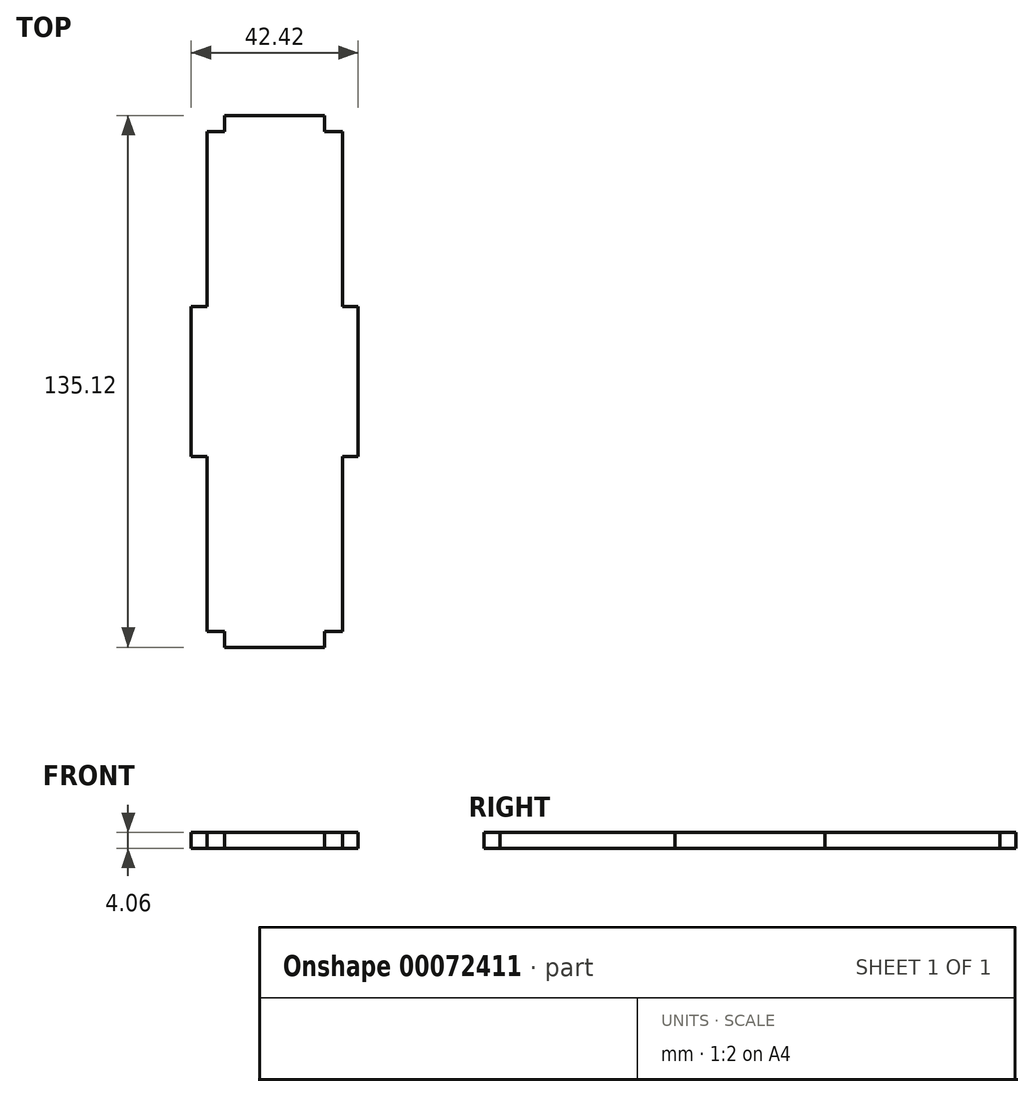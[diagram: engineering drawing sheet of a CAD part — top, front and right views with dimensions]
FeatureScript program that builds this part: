
annotation { "Feature Type Name" : "Feature", "Feature Type Description" : "" }
export const myFeature = defineFeature(function(context is Context, id is Id, definition is map)
    precondition{}
    {
        {
            var Q0;
            Q0=qCreatedBy(makeId("Top.planeOp"),FACE);
            var sketch = newSketch(context, id + "F0", { "sketchPlane" : qUnion([Q0])});
            skLineSegment(sketch, "E0.rect.bottom", {"start": v(17.14, 63.5) * mm, "end": v(-17.15, 63.5) * mm});
            skLineSegment(sketch, "E0.rect.top", {"start": v(17.14, -63.5) * mm, "end": v(-17.15, -63.5) * mm});
            skLineSegment(sketch, "E0.rect.left", {"start": v(17.15, 63.5) * mm, "end": v(17.15, -63.5) * mm});
            skLineSegment(sketch, "E0.rect.right", {"start": v(-17.15, 63.5) * mm, "end": v(-17.15, -63.5) * mm});
            skPoint(sketch, "E0.rect.middle", {"position": v(0, 0) * mm});
            skLineSegment(sketch, "E1.rect.bottom", {"start": v(12.7, -67.56) * mm, "end": v(-12.7, -67.56) * mm});
            skLineSegment(sketch, "E1.rect.top", {"start": v(12.7, -59.44) * mm, "end": v(-12.7, -59.44) * mm});
            skLineSegment(sketch, "E1.rect.left", {"start": v(12.7, -67.56) * mm, "end": v(12.7, -59.44) * mm});
            skLineSegment(sketch, "E1.rect.right", {"start": v(-12.7, -67.56) * mm, "end": v(-12.7, -59.44) * mm});
            skPoint(sketch, "E1.rect.middle", {"position": v(0, -63.5) * mm});
            skLineSegment(sketch, "E2", {"start": v(-58.3, 0) * mm, "end": v(70.6, 0) * mm, "construction": true});
            skLineSegment(sketch, "E3", {"start": v(0, 86.83) * mm, "end": v(0, -101.23) * mm, "construction": true});
            skPoint(sketch, "E3.startSnap0", {"position": v(0, 63.5) * mm});
            skLineSegment(sketch, "E4.MirrorCS", {"start": v(12.7, 59.44) * mm, "end": v(-12.7, 59.44) * mm});
            skLineSegment(sketch, "E5.MirrorCS", {"start": v(12.7, 67.56) * mm, "end": v(-12.7, 67.56) * mm});
            skLineSegment(sketch, "E6.MirrorCS", {"start": v(-12.7, 67.56) * mm, "end": v(-12.7, 59.44) * mm});
            skLineSegment(sketch, "E7.MirrorCS", {"start": v(12.7, 67.56) * mm, "end": v(12.7, 59.44) * mm});
            skLineSegment(sketch, "E8.rect.bottom", {"start": v(21.2, 19.05) * mm, "end": v(13.08, 19.05) * mm});
            skLineSegment(sketch, "E8.rect.top", {"start": v(21.2, -19.05) * mm, "end": v(13.08, -19.05) * mm});
            skLineSegment(sketch, "E8.rect.left", {"start": v(21.2, 19.05) * mm, "end": v(21.2, -19.05) * mm});
            skLineSegment(sketch, "E8.rect.right", {"start": v(13.08, 19.05) * mm, "end": v(13.08, -19.05) * mm});
            skPoint(sketch, "E8.rect.middle", {"position": v(17.15, 0) * mm});
            skLineSegment(sketch, "E9.MirrorCS", {"start": v(-13.08, 19.05) * mm, "end": v(-13.08, -19.05) * mm});
            skLineSegment(sketch, "E10.MirrorCS", {"start": v(-21.2, 19.05) * mm, "end": v(-13.08, 19.05) * mm});
            skLineSegment(sketch, "E11.MirrorCS", {"start": v(-21.2, 19.05) * mm, "end": v(-21.2, -19.05) * mm});
            skLineSegment(sketch, "E12.MirrorCS", {"start": v(-21.2, -19.05) * mm, "end": v(-13.08, -19.05) * mm});
            skSolve(sketch);
        }
        {
            var Q0;
            {var subQ5=sQuery(id+"F0.wireOp",EDGE,"E8.rect.left");Q0=makeQuery(id+"F0.imprint","IMPRINT",FACE,{"disambiguationData":[TD([[makeQuery(id+"F0.imprint","IMPRINT",EDGE,{"derivedFrom":subQ5}),-1.0]])]});}
            var Q1;
            {var subQ5=sQuery(id+"F0.wireOp",EDGE,"E4.MirrorCS");Q1=makeQuery(id+"F0.imprint","IMPRINT",FACE,{"disambiguationData":[TD([[makeQuery(id+"F0.imprint","IMPRINT",EDGE,{"derivedFrom":subQ5}),-1.0]])]});}
            var Q2;
            {var subQ5=sQuery(id+"F0.wireOp",EDGE,"E1.rect.bottom");Q2=makeQuery(id+"F0.imprint","IMPRINT",FACE,{"disambiguationData":[TD([[makeQuery(id+"F0.imprint","IMPRINT",EDGE,{"derivedFrom":subQ5}),-1.0]])]});}
            var Q3;
            {var subQ5=sQuery(id+"F0.wireOp",EDGE,"E1.rect.top");Q3=makeQuery(id+"F0.imprint","IMPRINT",FACE,{"disambiguationData":[TD([[makeQuery(id+"F0.imprint","IMPRINT",EDGE,{"derivedFrom":subQ5}),1.0]])]});}
            var Q4;
            {var subQ1=sQuery(id+"F0.wireOp",EDGE,"E1.rect.top");Q4=makeQuery(id+"F0.imprint","IMPRINT",FACE,{"disambiguationData":[TD([[makeQuery(id+"F0.imprint","IMPRINT",EDGE,{"derivedFrom":subQ1}),-1.0]])]});}
            var Q5;
            {var subQ5=sQuery(id+"F0.wireOp",EDGE,"E8.rect.right");Q5=makeQuery(id+"F0.imprint","IMPRINT",FACE,{"disambiguationData":[TD([[makeQuery(id+"F0.imprint","IMPRINT",EDGE,{"derivedFrom":subQ5}),1.0]])]});}
            var Q6;
            {var subQ5=sQuery(id+"F0.wireOp",EDGE,"E9.MirrorCS");Q6=makeQuery(id+"F0.imprint","IMPRINT",FACE,{"disambiguationData":[TD([[makeQuery(id+"F0.imprint","IMPRINT",EDGE,{"derivedFrom":subQ5}),-1.0]])]});}
            var Q7;
            {var subQ5=sQuery(id+"F0.wireOp",EDGE,"E5.MirrorCS");Q7=makeQuery(id+"F0.imprint","IMPRINT",FACE,{"disambiguationData":[TD([[makeQuery(id+"F0.imprint","IMPRINT",EDGE,{"derivedFrom":subQ5}),1.0]])]});}
            var Q8;
            {var subQ5=sQuery(id+"F0.wireOp",EDGE,"E11.MirrorCS");Q8=makeQuery(id+"F0.imprint","IMPRINT",FACE,{"disambiguationData":[TD([[makeQuery(id+"F0.imprint","IMPRINT",EDGE,{"derivedFrom":subQ5}),1.0]])]});}
            extrude(context, id + "F1", {"entities" : qUnion([Q0, Q1, Q2, Q3, Q4, Q5, Q6, Q7, Q8]), "depth" : 4.06 * mm});
        }
    });
